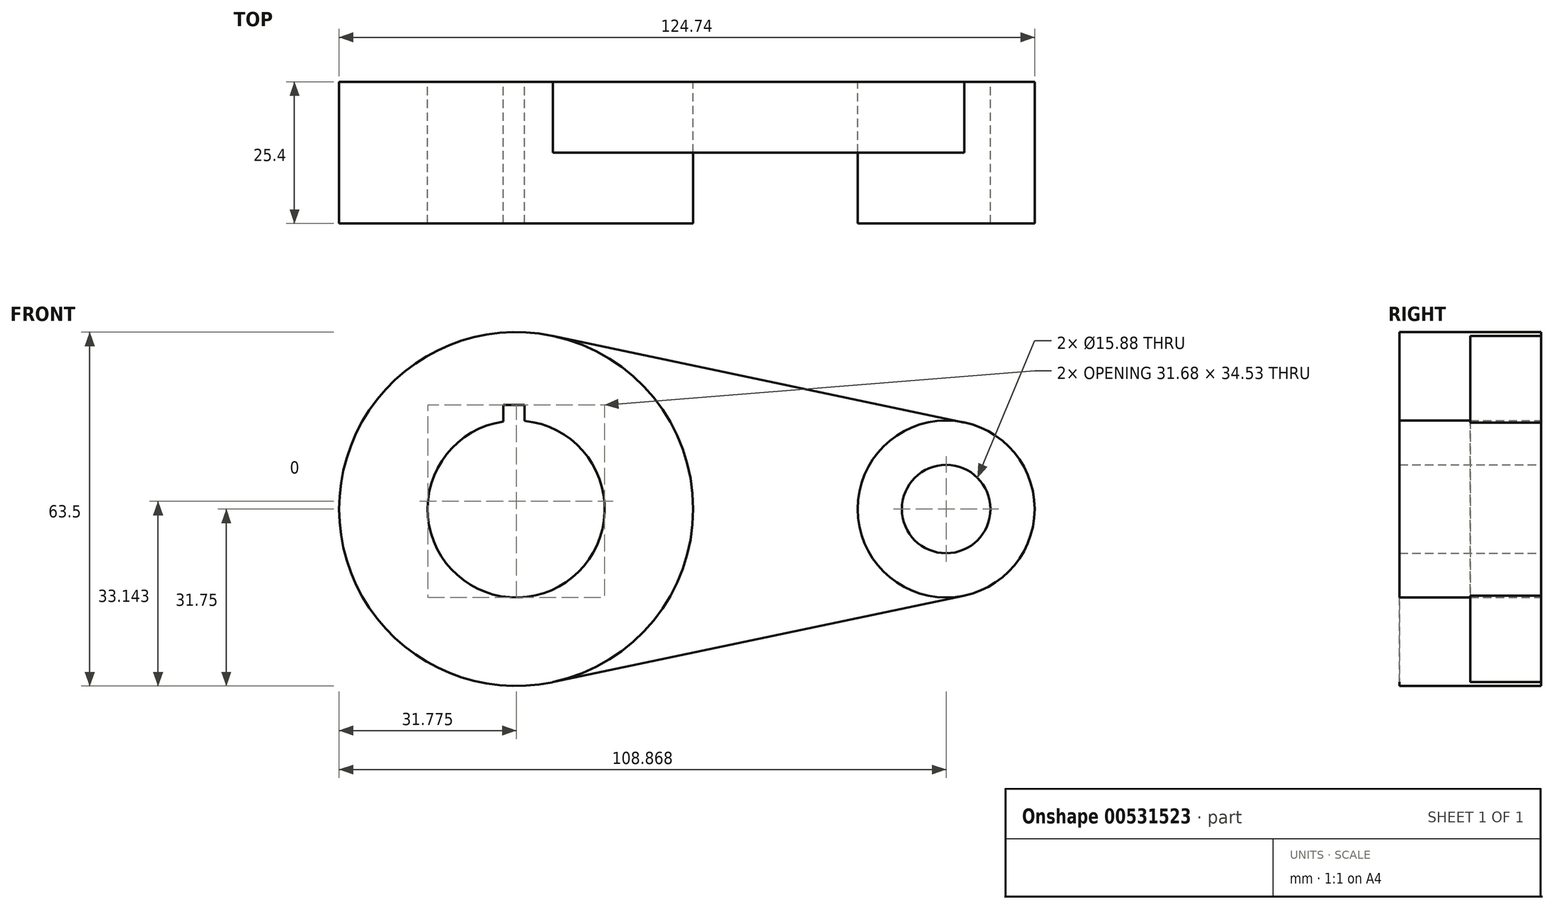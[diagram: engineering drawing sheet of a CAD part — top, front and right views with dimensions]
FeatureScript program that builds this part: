
annotation { "Feature Type Name" : "Feature", "Feature Type Description" : "" }
export const myFeature = defineFeature(function(context is Context, id is Id, definition is map)
    precondition{}
    {
        {
            var Q0;
            Q0=qCreatedBy(makeId("Front.planeOp"),FACE);
            var sketch = newSketch(context, id + "F0", { "sketchPlane" : qUnion([Q0])});
            skCircle(sketch, "E0", {"center": v(-42.75, 0) * mm, "radius": 31.75 * mm});
            skCircle(sketch, "E1", {"center": v(34.37, 0) * mm, "radius": 15.88 * mm});
            skLineSegment(sketch, "E2", {"start": v(-36.24, 31.08) * mm, "end": v(37.64, 15.54) * mm});
            skLineSegment(sketch, "E3", {"start": v(-36.24, -31.08) * mm, "end": v(37.64, -15.54) * mm});
            skCircle(sketch, "E4", {"center": v(-42.75, 0) * mm, "radius": 15.88 * mm});
            skCircle(sketch, "E5", {"center": v(34.37, 0) * mm, "radius": 7.94 * mm});
            skLineSegment(sketch, "E6.bottom", {"start": v(-41.25, 13.58) * mm, "end": v(-45.06, 13.58) * mm});
            skLineSegment(sketch, "E6.top", {"start": v(-41.25, 18.66) * mm, "end": v(-45.06, 18.66) * mm});
            skLineSegment(sketch, "E6.left", {"start": v(-41.25, 13.58) * mm, "end": v(-41.25, 18.66) * mm});
            skLineSegment(sketch, "E6.right", {"start": v(-45.06, 13.58) * mm, "end": v(-45.06, 18.66) * mm});
            skSolve(sketch);
        }
        {
            var Q0;
            {var subQ8=sQuery(id+"F0.wireOp",EDGE,"E6.top");Q0=makeQuery(id+"F0.imprint","IMPRINT",FACE,{"disambiguationData":[TD([[makeQuery(id+"F0.imprint","IMPRINT",EDGE,{"derivedFrom":subQ8}),-1.0]])]});}
            extrude(context, id + "F1", {"entities" : qUnion([Q0]), "depth" : 25.4 * mm, "offsetDistance" : 25.4 * mm});
        }
        {
            var Q0;
            Q0=makeQuery(id+"F0.imprint","IMPRINT",FACE,{"disambiguationData":[TD([[makeQuery(id+"F0.imprint","IMPRINT",EDGE,{"derivedFrom":sQuery(id+"F0.wireOp",EDGE,"E5")}),-1.0]])]});
            extrude(context, id + "F2", {"entities" : qUnion([Q0]), "depth" : 25.4 * mm, "offsetDistance" : 25.4 * mm});
        }
        {
            var Q0;
            {var subQ0=sQuery(id+"F0.wireOp",EDGE,"E2");Q0=makeQuery(id+"F0.imprint","IMPRINT",FACE,{"disambiguationData":[TD([[makeQuery(id+"F0.imprint","IMPRINT",EDGE,{"derivedFrom":subQ0}),-1.0]])]});}
            extrude(context, id + "F3", {"entities" : qUnion([Q0]), "depth" : 12.7 * mm, "offsetDistance" : 25.4 * mm});
        }
    });
